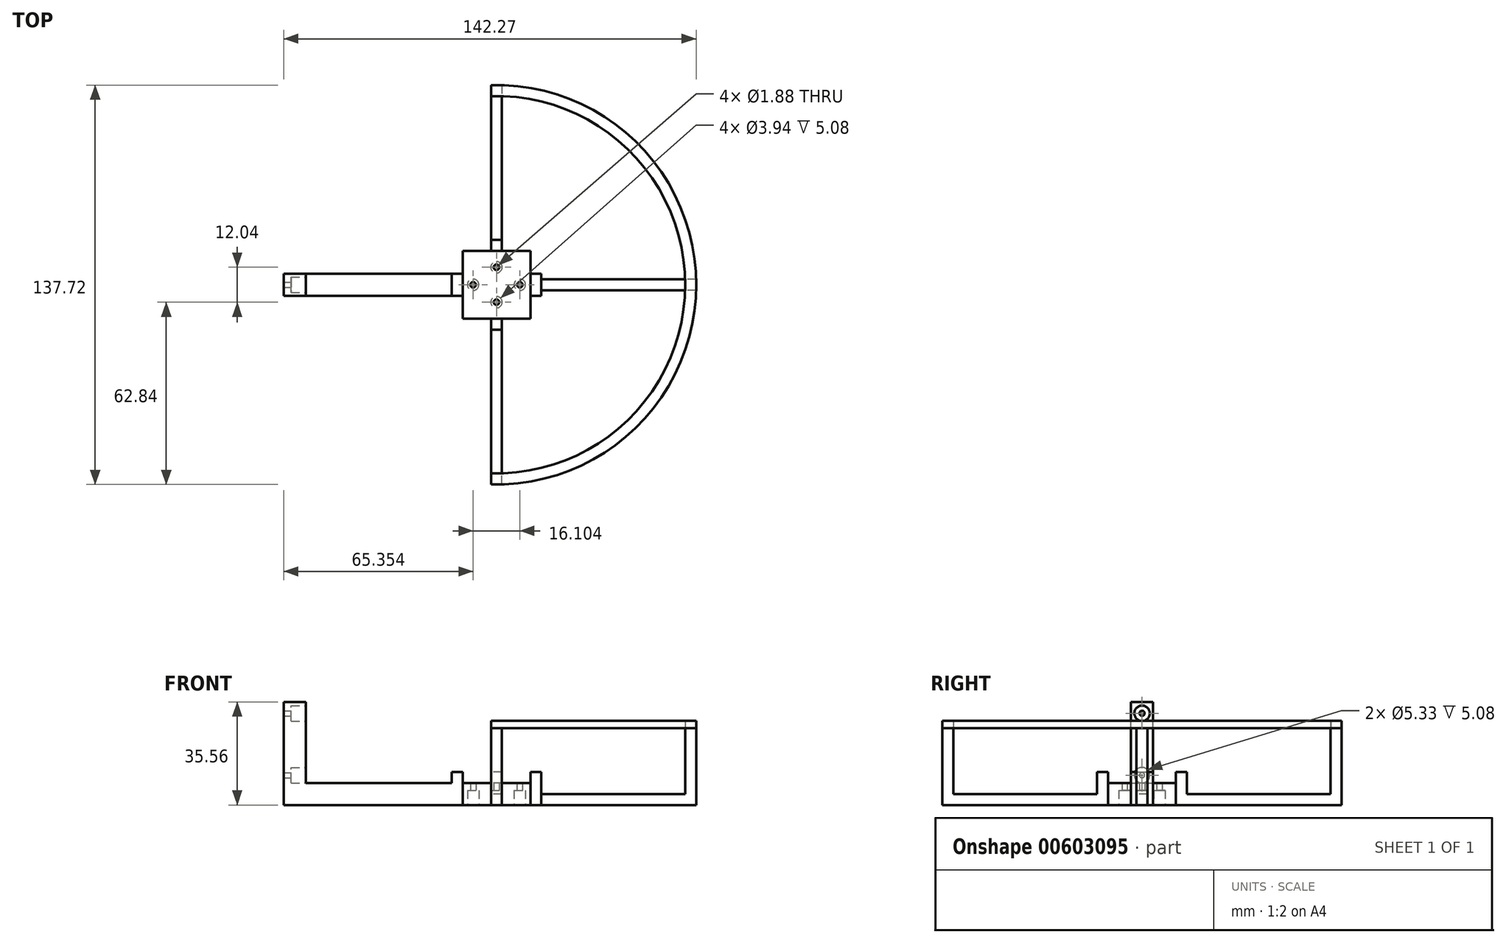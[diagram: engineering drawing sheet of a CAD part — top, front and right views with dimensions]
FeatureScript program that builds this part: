
annotation { "Feature Type Name" : "Feature", "Feature Type Description" : "" }
export const myFeature = defineFeature(function(context is Context, id is Id, definition is map)
    precondition{}
    {
        {
            var Q0;
            Q0=qCreatedBy(makeId("Front.planeOp"),FACE);
            var sketch = newSketch(context, id + "F0", { "sketchPlane" : qUnion([Q0])});
            skLineSegment(sketch, "E0.bottom", {"start": v(0, 0) * mm, "end": v(7.62, 0) * mm});
            skLineSegment(sketch, "E0.top", {"start": v(0, 35.56) * mm, "end": v(7.62, 35.56) * mm});
            skLineSegment(sketch, "E0.left", {"start": v(0, 0) * mm, "end": v(0, 35.56) * mm});
            skLineSegment(sketch, "E0.right", {"start": v(7.62, 0) * mm, "end": v(7.62, 35.56) * mm});
            skLineSegment(sketch, "E1.bottom", {"start": v(0, 0) * mm, "end": v(88.9, 0) * mm});
            skLineSegment(sketch, "E1.top", {"start": v(0, 7.62) * mm, "end": v(88.9, 7.62) * mm});
            skLineSegment(sketch, "E1.left", {"start": v(0, 0) * mm, "end": v(0, 7.62) * mm});
            skLineSegment(sketch, "E1.right", {"start": v(88.9, 0) * mm, "end": v(88.9, 7.62) * mm});
            skLineSegment(sketch, "E2.bottom", {"start": v(88.9, 7.62) * mm, "end": v(85.1, 7.62) * mm});
            skLineSegment(sketch, "E2.top", {"start": v(88.9, 11.43) * mm, "end": v(85.1, 11.43) * mm});
            skLineSegment(sketch, "E2.left", {"start": v(88.9, 7.62) * mm, "end": v(88.9, 11.43) * mm});
            skLineSegment(sketch, "E2.right", {"start": v(85.1, 7.62) * mm, "end": v(85.1, 11.43) * mm});
            skLineSegment(sketch, "E3.bottom", {"start": v(61.72, 7.62) * mm, "end": v(57.91, 7.62) * mm});
            skLineSegment(sketch, "E3.top", {"start": v(61.72, 11.43) * mm, "end": v(57.91, 11.43) * mm});
            skLineSegment(sketch, "E3.left", {"start": v(61.72, 7.62) * mm, "end": v(61.72, 11.43) * mm});
            skLineSegment(sketch, "E3.right", {"start": v(57.91, 7.62) * mm, "end": v(57.91, 11.43) * mm});
            skPoint(sketch, "E4.oppositeSnap0", {"position": v(7.62, 17.78) * mm});
            skSolve(sketch);
        }
        {
            var Q0;
            Q0 = qSketchRegion(id + "F0", true);
            extrude(context, id + "F1", {"entities" : qUnion([Q0]), "endBound" : BoundingType.SYMMETRIC, "depth" : 7.62 * mm, "offsetDistance" : 25.4 * mm});
        }
        {
            var Q0;
            {var subQ0=sQuery(id+"F0.wireOp",EDGE,"E1.top");Q0=makeQuery(id+"F1.opExtrude","SWEPT_FACE",FACE,{"disambiguationData":[OSD([subQ0]),TDD([makeQuery(id+"F0.imprint","IMPRINT",EDGE,{"disambiguationData":[TD([[makeQuery(id+"F0.imprint","INTERSECT",VERTEX,{"derivedFrom":[subQ0,sQuery(id+"F0.wireOp",EDGE,"E2.bottom"),sQuery(id+"F0.wireOp",EDGE,"E2.right")]}),1.0]])],"derivedFrom":subQ0})])]});}
            var sketch = newSketch(context, id + "F2", { "sketchPlane" : qUnion([Q0])});
            skLineSegment(sketch, "E5", {"start": v(61.72, 0) * mm, "end": v(85.1, 0) * mm});
            skLineSegment(sketch, "E6.bottom", {"start": v(85.1, -11.68) * mm, "end": v(61.72, -11.68) * mm});
            skLineSegment(sketch, "E6.top", {"start": v(85.1, 11.68) * mm, "end": v(61.72, 11.68) * mm});
            skLineSegment(sketch, "E6.left", {"start": v(85.1, -11.68) * mm, "end": v(85.1, 11.68) * mm});
            skLineSegment(sketch, "E6.right", {"start": v(61.72, -11.68) * mm, "end": v(61.72, 11.68) * mm});
            skPoint(sketch, "E6.middle", {"position": v(73.4, 0) * mm});
            skSolve(sketch);
        }
        {
            var Q0;
            Q0 = qSketchRegion(id + "F2", true);
            extrude(context, id + "F3", {"entities" : qUnion([Q0]), "operationType" : NewBodyOperationType.ADD, "oppositeDirection" : true, "depth" : 7.62 * mm, "offsetDistance" : 25.4 * mm});
        }
        {
            var Q0;
            Q0=makeQuery(id+"F3.opExtrude","SWEPT_FACE",FACE,{"disambiguationData":[OSD([sQuery(id+"F2.wireOp",EDGE,"E6.bottom")])]});
            var sketch = newSketch(context, id + "F4", { "sketchPlane" : qUnion([Q0])});
            skLineSegment(sketch, "E7", {"start": v(73.4, 7.62) * mm, "end": v(73.4, 0) * mm});
            skLineSegment(sketch, "E8.bottom", {"start": v(75.31, 0) * mm, "end": v(71.5, 0) * mm});
            skLineSegment(sketch, "E8.top", {"start": v(75.31, 11.43) * mm, "end": v(71.5, 11.43) * mm});
            skLineSegment(sketch, "E8.left", {"start": v(75.31, 0) * mm, "end": v(75.31, 11.43) * mm});
            skLineSegment(sketch, "E8.right", {"start": v(71.5, 0) * mm, "end": v(71.5, 11.43) * mm});
            skPoint(sketch, "E8.middle", {"position": v(73.4, 5.72) * mm});
            skSolve(sketch);
        }
        {
            var Q0;
            Q0 = qSketchRegion(id + "F4", true);
            extrude(context, id + "F5", {"entities" : qUnion([Q0]), "operationType" : NewBodyOperationType.ADD, "depth" : 3.8 * mm, "offsetDistance" : 25.4 * mm});
        }
        {
            var Q0;
            Q0=makeQuery(id+"F3.opExtrude","SWEPT_FACE",FACE,{"disambiguationData":[OSD([sQuery(id+"F2.wireOp",EDGE,"E6.top")])]});
            var sketch = newSketch(context, id + "F6", { "sketchPlane" : qUnion([Q0])});
            skLineSegment(sketch, "E9", {"start": v(-73.4, 7.62) * mm, "end": v(-73.4, 0) * mm});
            skLineSegment(sketch, "E10.bottom", {"start": v(-71.5, 0) * mm, "end": v(-75.31, 0) * mm});
            skLineSegment(sketch, "E10.top", {"start": v(-71.5, 11.43) * mm, "end": v(-75.31, 11.43) * mm});
            skLineSegment(sketch, "E10.left", {"start": v(-71.5, 0) * mm, "end": v(-71.5, 11.43) * mm});
            skLineSegment(sketch, "E10.right", {"start": v(-75.31, 0) * mm, "end": v(-75.31, 11.43) * mm});
            skPoint(sketch, "E10.middle", {"position": v(-73.4, 5.72) * mm});
            skSolve(sketch);
        }
        {
            var Q0;
            Q0 = qSketchRegion(id + "F6", true);
            extrude(context, id + "F7", {"entities" : qUnion([Q0]), "operationType" : NewBodyOperationType.ADD, "depth" : 3.8 * mm, "offsetDistance" : 25.4 * mm});
        }
        {
            var Q0;
            Q0=makeQuery(id+"F1.opExtrude","SWEPT_FACE",FACE,{"disambiguationData":[OSD([sQuery(id+"F0.wireOp",EDGE,"E0.right")])]});
            var sketch = newSketch(context, id + "F8", { "sketchPlane" : qUnion([Q0])});
            skCircle(sketch, "E11", {"center": v(0, 31.62) * mm, "radius": 2.67 * mm});
            skCircle(sketch, "E12", {"center": v(0, 10.29) * mm, "radius": 2.67 * mm});
            skPoint(sketch, "E13", {"position": v(0, 35.56) * mm});
            skSolve(sketch);
        }
        {
            var Q0;
            Q0=sQuery(id+"F8.wireOp",VERTEX,"E11.center");
            var Q1;
            Q1=sQuery(id+"F8.wireOp",VERTEX,"E12.center");
            var Q2;
            Q2=makeQuery(id+"F1.opExtrude","SWEPT_BODY",BODY,{"disambiguationData":[OSD([sQuery(id+"F0.wireOp",EDGE,"E0.top"),sQuery(id+"F0.wireOp",EDGE,"E0.left"),sQuery(id+"F0.wireOp",EDGE,"E0.right"),sQuery(id+"F0.wireOp",EDGE,"E1.bottom"),sQuery(id+"F0.wireOp",EDGE,"E1.top"),sQuery(id+"F0.wireOp",EDGE,"E1.left"),sQuery(id+"F0.wireOp",EDGE,"E1.right"),sQuery(id+"F0.wireOp",EDGE,"E2.top"),sQuery(id+"F0.wireOp",EDGE,"E2.left"),sQuery(id+"F0.wireOp",EDGE,"E2.right"),sQuery(id+"F0.wireOp",EDGE,"E3.top"),sQuery(id+"F0.wireOp",EDGE,"E3.left"),sQuery(id+"F0.wireOp",EDGE,"E3.right")])]});
            hole(context, id + "F9", {"style" : HoleStyle.C_BORE, "endStyle" : HoleEndStyle.BLIND, "holeDiameter" : 1.78 * mm, "cBoreDiameter" : 5.33 * mm, "cBoreDepth" : 5.08 * mm, "majorDiameter" : 6.35 * mm, "holeDepth" : 8.9 * mm, "isTappedThrough" : true, "tappedDepth" : 12.7 * mm, "tapClearance" : 3, "locations" : qUnion([Q0, Q1]), "scope" : qUnion([Q2])});
        }
        {
            var Q0;
            Q0=makeQuery(id+"F7.boolean.opBoolean","MERGE",FACE,{"derivedFrom":[makeQuery(id+"F5.boolean.opBoolean","MERGE",FACE,{"derivedFrom":[makeQuery(id+"F3.boolean.opBoolean","MERGE",FACE,{"derivedFrom":[makeQuery(id+"F1.opExtrude","SWEPT_FACE",FACE,{"disambiguationData":[OSD([sQuery(id+"F0.wireOp",EDGE,"E1.bottom")])]}),makeQuery(id+"F3.opExtrude","CAP_FACE",FACE,{"disambiguationData":[OSD([sQuery(id+"F2.wireOp",EDGE,"E6.bottom"),sQuery(id+"F2.wireOp",EDGE,"E6.top"),sQuery(id+"F2.wireOp",EDGE,"E6.left"),sQuery(id+"F2.wireOp",EDGE,"E6.right")])],"isStart":false})]}),makeQuery(id+"F5.opExtrude","SWEPT_FACE",FACE,{"disambiguationData":[OSD([sQuery(id+"F4.wireOp",EDGE,"E8.bottom")])]})]}),makeQuery(id+"F7.opExtrude","SWEPT_FACE",FACE,{"disambiguationData":[OSD([sQuery(id+"F6.wireOp",EDGE,"E10.bottom")])]})]});
            var sketch = newSketch(context, id + "F10", { "sketchPlane" : qUnion([Q0])});
            skLineSegment(sketch, "E14", {"start": v(73.4, 15.5) * mm, "end": v(73.4, -15.5) * mm});
            skLineSegment(sketch, "E15", {"start": v(88.9, 0) * mm, "end": v(0, 0) * mm});
            skCircle(sketch, "E16", {"center": v(81.46, 0) * mm, "radius": 1.97 * mm});
            skCircle(sketch, "E17", {"center": v(65.35, 0) * mm, "radius": 1.97 * mm});
            skCircle(sketch, "E18", {"center": v(73.4, 6.02) * mm, "radius": 1.97 * mm});
            skCircle(sketch, "E19", {"center": v(73.4, -6.02) * mm, "radius": 1.97 * mm});
            skSolve(sketch);
        }
        {
            var Q0;
            Q0=sQuery(id+"F10.wireOp",VERTEX,"E18.center");
            var Q1;
            Q1=sQuery(id+"F10.wireOp",VERTEX,"E17.center");
            var Q2;
            Q2=sQuery(id+"F10.wireOp",VERTEX,"E19.center");
            var Q3;
            Q3=sQuery(id+"F10.wireOp",VERTEX,"E16.center");
            var Q4;
            Q4=makeQuery(id+"F1.opExtrude","SWEPT_BODY",BODY,{"disambiguationData":[OSD([sQuery(id+"F0.wireOp",EDGE,"E0.top"),sQuery(id+"F0.wireOp",EDGE,"E0.left"),sQuery(id+"F0.wireOp",EDGE,"E0.right"),sQuery(id+"F0.wireOp",EDGE,"E1.bottom"),sQuery(id+"F0.wireOp",EDGE,"E1.top"),sQuery(id+"F0.wireOp",EDGE,"E1.left"),sQuery(id+"F0.wireOp",EDGE,"E1.right"),sQuery(id+"F0.wireOp",EDGE,"E2.top"),sQuery(id+"F0.wireOp",EDGE,"E2.left"),sQuery(id+"F0.wireOp",EDGE,"E2.right"),sQuery(id+"F0.wireOp",EDGE,"E3.top"),sQuery(id+"F0.wireOp",EDGE,"E3.left"),sQuery(id+"F0.wireOp",EDGE,"E3.right")])]});
            hole(context, id + "F11", {"style" : HoleStyle.C_BORE, "endStyle" : HoleEndStyle.BLIND, "holeDiameter" : 1.88 * mm, "cBoreDiameter" : 3.94 * mm, "cBoreDepth" : 5.08 * mm, "majorDiameter" : 6.35 * mm, "holeDepth" : 8.9 * mm, "isTappedThrough" : true, "tappedDepth" : 12.7 * mm, "tapClearance" : 3, "locations" : qUnion([Q0, Q1, Q2, Q3]), "scope" : qUnion([Q4])});
        }
        {
            var Q0;
            Q0=makeQuery(id+"F1.opExtrude","SWEPT_FACE",FACE,{"disambiguationData":[OSD([sQuery(id+"F0.wireOp",EDGE,"E1.right"),sQuery(id+"F0.wireOp",EDGE,"E2.left")])]});
            var sketch = newSketch(context, id + "F12", { "sketchPlane" : qUnion([Q0])});
            skLineSegment(sketch, "E20.bottom", {"start": v(1.9, 0) * mm, "end": v(-1.9, 0) * mm});
            skLineSegment(sketch, "E20.top", {"start": v(1.9, 3.81) * mm, "end": v(-1.9, 3.81) * mm});
            skLineSegment(sketch, "E20.left", {"start": v(1.9, 0) * mm, "end": v(1.9, 3.81) * mm});
            skLineSegment(sketch, "E20.right", {"start": v(-1.9, 0) * mm, "end": v(-1.9, 3.81) * mm});
            skPoint(sketch, "E20.middle", {"position": v(0, 1.9) * mm});
            skSolve(sketch);
        }
        {
            var Q0;
            Q0 = qSketchRegion(id + "F12", true);
            extrude(context, id + "F13", {"entities" : qUnion([Q0]), "operationType" : NewBodyOperationType.ADD, "depth" : 53.34 * mm, "offsetDistance" : 25.4 * mm});
        }
        {
            var Q0;
            Q0=makeQuery(id+"F5.opExtrude","CAP_FACE",FACE,{"disambiguationData":[OSD([sQuery(id+"F4.wireOp",EDGE,"E8.bottom"),sQuery(id+"F4.wireOp",EDGE,"E8.top"),sQuery(id+"F4.wireOp",EDGE,"E8.left"),sQuery(id+"F4.wireOp",EDGE,"E8.right")])],"isStart":false});
            var sketch = newSketch(context, id + "F14", { "sketchPlane" : qUnion([Q0])});
            skLineSegment(sketch, "E21.bottom", {"start": v(75.31, 0) * mm, "end": v(71.5, 0) * mm});
            skLineSegment(sketch, "E21.top", {"start": v(75.31, 3.81) * mm, "end": v(71.5, 3.81) * mm});
            skLineSegment(sketch, "E21.left", {"start": v(75.31, 0) * mm, "end": v(75.31, 3.81) * mm});
            skLineSegment(sketch, "E21.right", {"start": v(71.5, 0) * mm, "end": v(71.5, 3.81) * mm});
            skPoint(sketch, "E21.middle", {"position": v(73.4, 1.9) * mm});
            skSolve(sketch);
        }
        {
            var Q0;
            Q0 = qSketchRegion(id + "F14", true);
            extrude(context, id + "F15", {"entities" : qUnion([Q0]), "operationType" : NewBodyOperationType.ADD, "depth" : 53.34 * mm, "offsetDistance" : 25.4 * mm});
        }
        {
            var Q0;
            Q0=makeQuery(id+"F7.opExtrude","CAP_FACE",FACE,{"disambiguationData":[OSD([sQuery(id+"F6.wireOp",EDGE,"E10.bottom"),sQuery(id+"F6.wireOp",EDGE,"E10.top"),sQuery(id+"F6.wireOp",EDGE,"E10.left"),sQuery(id+"F6.wireOp",EDGE,"E10.right")])],"isStart":false});
            var sketch = newSketch(context, id + "F16", { "sketchPlane" : qUnion([Q0])});
            skLineSegment(sketch, "E22.bottom", {"start": v(-71.5, 0) * mm, "end": v(-75.31, 0) * mm});
            skLineSegment(sketch, "E22.top", {"start": v(-71.5, 3.81) * mm, "end": v(-75.31, 3.81) * mm});
            skLineSegment(sketch, "E22.left", {"start": v(-71.5, 0) * mm, "end": v(-71.5, 3.81) * mm});
            skLineSegment(sketch, "E22.right", {"start": v(-75.31, 0) * mm, "end": v(-75.31, 3.81) * mm});
            skPoint(sketch, "E22.middle", {"position": v(-73.4, 1.9) * mm});
            skSolve(sketch);
        }
        {
            var Q0;
            Q0 = qSketchRegion(id + "F16", true);
            extrude(context, id + "F17", {"entities" : qUnion([Q0]), "operationType" : NewBodyOperationType.ADD, "depth" : 53.34 * mm, "offsetDistance" : 25.4 * mm});
        }
        {
            var Q0;
            Q0=makeQuery(id+"F17.opExtrude","SWEPT_FACE",FACE,{"disambiguationData":[OSD([sQuery(id+"F16.wireOp",EDGE,"E22.top")])]});
            var sketch = newSketch(context, id + "F18", { "sketchPlane" : qUnion([Q0])});
            skLineSegment(sketch, "E23.bottom", {"start": v(75.31, 65.02) * mm, "end": v(71.5, 65.02) * mm});
            skLineSegment(sketch, "E23.top", {"start": v(75.31, 68.83) * mm, "end": v(71.5, 68.83) * mm});
            skLineSegment(sketch, "E23.left", {"start": v(75.31, 65.02) * mm, "end": v(75.31, 68.83) * mm});
            skLineSegment(sketch, "E23.right", {"start": v(71.5, 65.02) * mm, "end": v(71.5, 68.83) * mm});
            skPoint(sketch, "E23.middle", {"position": v(73.4, 66.93) * mm});
            skLineSegment(sketch, "E24.bottom", {"start": v(142.24, -1.9) * mm, "end": v(138.43, -1.9) * mm});
            skLineSegment(sketch, "E24.top", {"start": v(142.24, 1.9) * mm, "end": v(138.43, 1.9) * mm});
            skLineSegment(sketch, "E24.left", {"start": v(142.24, -1.9) * mm, "end": v(142.24, 1.9) * mm});
            skLineSegment(sketch, "E24.right", {"start": v(138.43, -1.9) * mm, "end": v(138.43, 1.9) * mm});
            skPoint(sketch, "E24.middle", {"position": v(140.34, 0) * mm});
            skLineSegment(sketch, "E25.bottom", {"start": v(75.31, -68.83) * mm, "end": v(71.5, -68.83) * mm});
            skLineSegment(sketch, "E25.top", {"start": v(75.31, -65.02) * mm, "end": v(71.5, -65.02) * mm});
            skLineSegment(sketch, "E25.left", {"start": v(75.31, -68.83) * mm, "end": v(75.31, -65.02) * mm});
            skLineSegment(sketch, "E25.right", {"start": v(71.5, -68.83) * mm, "end": v(71.5, -65.02) * mm});
            skPoint(sketch, "E25.middle", {"position": v(73.4, -66.93) * mm});
            skSolve(sketch);
        }
        {
            var Q0;
            Q0 = qSketchRegion(id + "F18", true);
            extrude(context, id + "F19", {"entities" : qUnion([Q0]), "operationType" : NewBodyOperationType.ADD, "depth" : 22.73 * mm, "offsetDistance" : 25.4 * mm});
        }
        {
            var Q0;
            Q0=makeQuery(id+"F19.opExtrude","CAP_FACE",FACE,{"disambiguationData":[OSD([sQuery(id+"F18.wireOp",EDGE,"E24.bottom"),sQuery(id+"F18.wireOp",EDGE,"E24.top"),sQuery(id+"F18.wireOp",EDGE,"E24.left"),sQuery(id+"F18.wireOp",EDGE,"E24.right")])],"isStart":false});
            var sketch = newSketch(context, id + "F20", { "sketchPlane" : qUnion([Q0])});
            skArc(sketch, "E26", {"start": v(71.5, 68.83) * mm, "mid": v(142.27, 0) * mm, "end": v(71.5, -68.83) * mm});
            skArc(sketch, "E27", {"start": v(71.5, 65.02) * mm, "mid": v(138.46, 0) * mm, "end": v(71.5, -65.02) * mm});
            skLineSegment(sketch, "E28", {"start": v(71.5, 65.02) * mm, "end": v(71.5, 68.83) * mm});
            skLineSegment(sketch, "E29", {"start": v(71.5, -65.02) * mm, "end": v(71.5, -68.83) * mm});
            skSolve(sketch);
        }
        {
            var Q0;
            Q0 = qSketchRegion(id + "F20", true);
            extrude(context, id + "F21", {"entities" : qUnion([Q0]), "operationType" : NewBodyOperationType.ADD, "depth" : 2.54 * mm, "offsetDistance" : 25.4 * mm});
        }
    });
